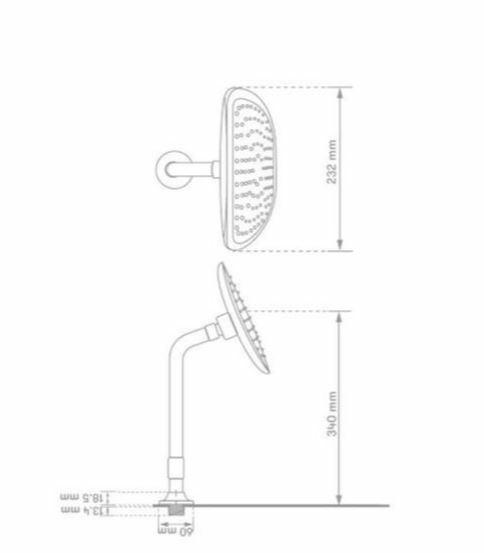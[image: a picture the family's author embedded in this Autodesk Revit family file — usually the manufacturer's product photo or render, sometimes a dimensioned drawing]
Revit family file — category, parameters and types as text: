
# Revit family: 01-1335-11 MEZCLADOR DUCHA 8” SIN SALIDA ATLANTICO
name_source: partatom
category: Plumbing Fixtures
revit_build: Autodesk Revit 2018 (Build: 20170223_1515(x64)
units: mm (PartAtom-declared; Revit-internal decimal feet)

## family parameters
Cut with Voids When Loaded = No
Host = Face
OmniClass Number = 23.31.11.00
Part Type = Normal
Room Calculation Point = No
Round Connector Dimension = Use Diameter
Shared = No

## types (1)
- 01-1335-11
    Alto Manija = 85 mm  [stored 0.278871 ft]
    Ancho manija = 66 mm
    CW Connection = Yes
    Default Elevation = 0 mm  [stored 0 ft]
    Description = Mezclador ducha
    Distancia entre griferias = 203 mm
    Escudo = 60 mm  [stored 0.19685 ft]
    HW Connection = Yes
    Link Ficha Tecnica = https://infotecnica.gricol.com
    Manufacturer = Gricol
    Metal Laton = Metal Laton Cromado
    Model = 01-1335-11
    Plastico ABS Cromado = Plastico - ABS Cromado
    Product Name = MEZCLADOR DUCHA 8” SIN SALIDA ATLANTICO
    Type Image = <None>
    URL = https://www.gricol.com
    Vent Connection = No
    Waste Connection = No

note: [stored X ft] marks values corroborated as IEEE doubles in the binary element streams (Revit-internal decimal feet)

## geometry (parser evidence)
native form markers: Blend x2, Sweep x26
no freeform markers — native parametric forms only
